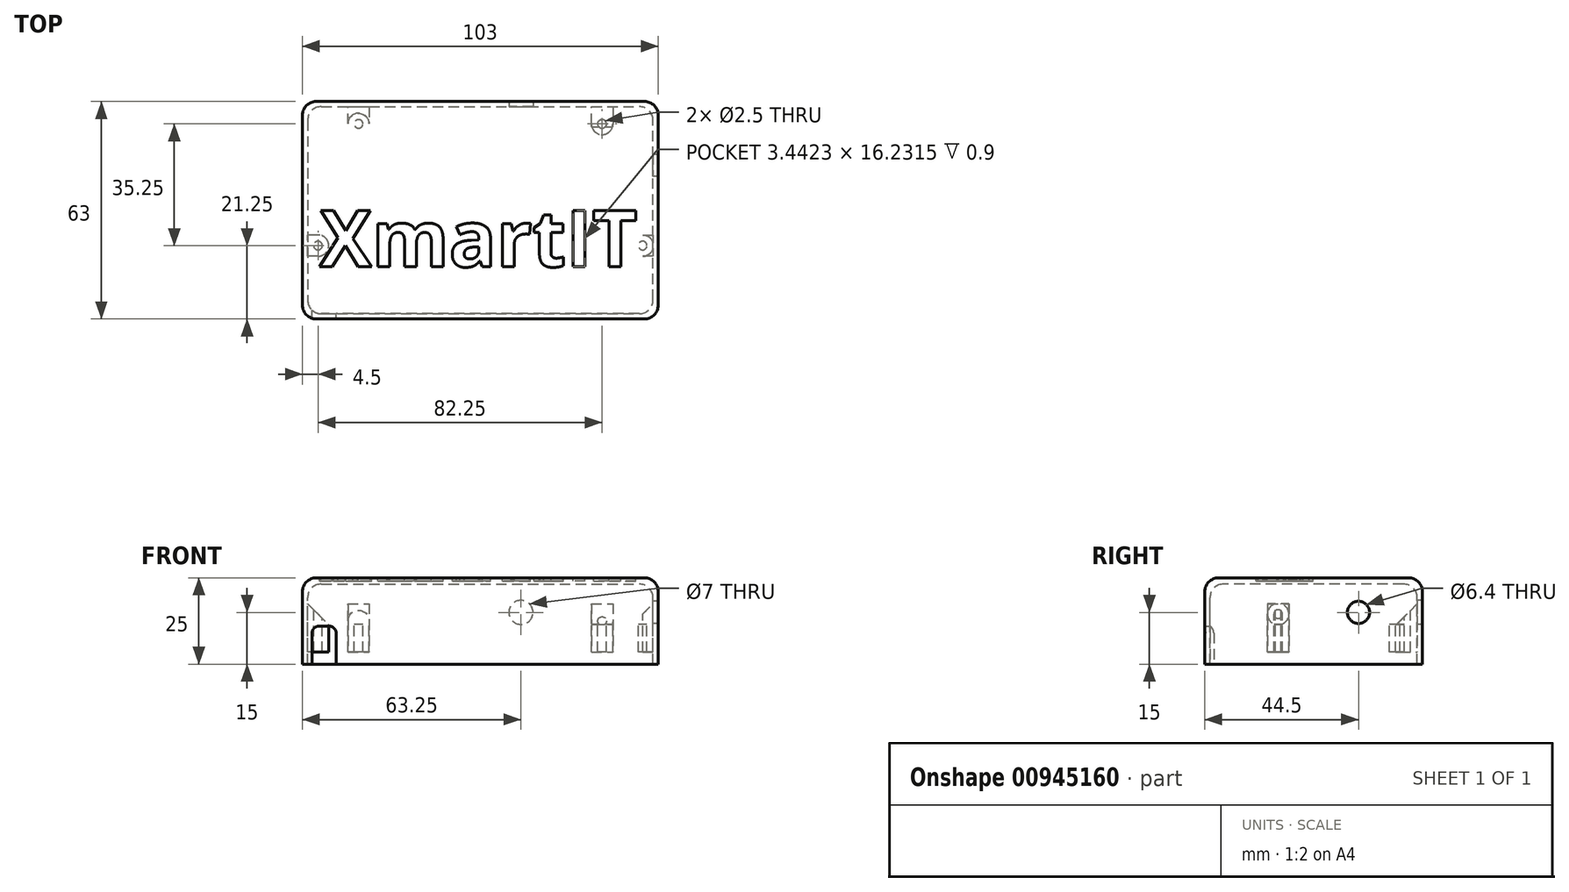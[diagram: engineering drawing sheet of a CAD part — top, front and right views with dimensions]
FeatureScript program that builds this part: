
annotation { "Feature Type Name" : "Feature", "Feature Type Description" : "" }
export const myFeature = defineFeature(function(context is Context, id is Id, definition is map)
    precondition{}
    {
        {
            assignVariable(context, id + "F0", {"name" : "Paredes", "anyValue" : 1.5});
        }
        {
            var Q0;
            Q0=qCreatedBy(makeId("Top.planeOp"),FACE);
            var sketch = newSketch(context, id + "F1", { "sketchPlane" : qUnion([Q0])});
            skLineSegment(sketch, "E0.bottom", {"start": v(50, -30) * mm, "end": v(-50, -30) * mm});
            skLineSegment(sketch, "E0.top", {"start": v(50, 30) * mm, "end": v(-50, 30) * mm});
            skLineSegment(sketch, "E0.left", {"start": v(50, -30) * mm, "end": v(50, 30) * mm});
            skLineSegment(sketch, "E0.right", {"start": v(-50, -30) * mm, "end": v(-50, 30) * mm});
            skPoint(sketch, "E0.middle", {"position": v(0, 0) * mm});
            skLineSegment(sketch, "E1.bottom", {"start": v(51.5, -31.5) * mm, "end": v(-51.5, -31.5) * mm});
            skLineSegment(sketch, "E1.top", {"start": v(51.5, 31.5) * mm, "end": v(-51.5, 31.5) * mm});
            skLineSegment(sketch, "E1.left", {"start": v(51.5, -31.5) * mm, "end": v(51.5, 31.5) * mm});
            skLineSegment(sketch, "E1.right", {"start": v(-51.5, -31.5) * mm, "end": v(-51.5, 31.5) * mm});
            skLineSegment(sketch, "E2.bottom", {"start": v(72.1, -40) * mm, "end": v(-72.1, -40) * mm});
            skLineSegment(sketch, "E2.top", {"start": v(72.1, 40) * mm, "end": v(-72.1, 40) * mm});
            skLineSegment(sketch, "E2.left", {"start": v(72.1, -40) * mm, "end": v(72.1, 40) * mm});
            skLineSegment(sketch, "E2.right", {"start": v(-72.1, -40) * mm, "end": v(-72.1, 40) * mm});
            skLineSegment(sketch, "E3", {"start": v(-51.5, 31.5) * mm, "end": v(-51.5, 40) * mm});
            skLineSegment(sketch, "E4", {"start": v(-51.5, -31.5) * mm, "end": v(-51.5, -40) * mm});
            skLineSegment(sketch, "E5", {"start": v(-41.73, -30) * mm, "end": v(-41.73, -4) * mm, "construction": true});
            skLineSegment(sketch, "E6.bottom", {"start": v(-50, -4) * mm, "end": v(50, -4) * mm});
            skLineSegment(sketch, "E6.top", {"start": v(-50, -2.2) * mm, "end": v(50, -2.2) * mm});
            skLineSegment(sketch, "E6.left", {"start": v(-50, -4) * mm, "end": v(-50, -2.2) * mm});
            skLineSegment(sketch, "E6.right", {"start": v(50, -4) * mm, "end": v(50, -2.2) * mm});
            skLineSegment(sketch, "E7.bottom", {"start": v(-55.7, -5) * mm, "end": v(-51.5, -5) * mm});
            skLineSegment(sketch, "E7.top", {"start": v(-55.7, 5) * mm, "end": v(-51.5, 5) * mm});
            skLineSegment(sketch, "E7.left", {"start": v(-55.7, -5) * mm, "end": v(-55.7, 5) * mm});
            skPoint(sketch, "E7.middle", {"position": v(-51.5, 0) * mm});
            skPoint(sketch, "E7.right.start.orphan", {"position": v(-47.3, -5) * mm});
            skPoint(sketch, "E8.trimOffspring.end.orphan", {"position": v(-47.3, 5) * mm});
            skLineSegment(sketch, "E9.bottom", {"start": v(72.1, -40) * mm, "end": v(84.1, -40) * mm});
            skLineSegment(sketch, "E9.top", {"start": v(72.1, -28) * mm, "end": v(84.1, -28) * mm});
            skLineSegment(sketch, "E9.left", {"start": v(72.1, -40) * mm, "end": v(72.1, -28) * mm});
            skLineSegment(sketch, "E9.right", {"start": v(87.1, -37) * mm, "end": v(87.1, -31) * mm});
            skCircle(sketch, "E10", {"center": v(79.6, -34) * mm, "radius": 1.5 * mm});
            skPoint(sketch, "E10.centerSnap0", {"position": v(87.1, -34) * mm});
            skPoint(sketch, "E10.centerSnap1", {"position": v(79.6, -28) * mm});
            skPoint(sketch, "E11.visualSharp", {"position": v(87.1, -28) * mm});
            skArc(sketch, "E11.filletArc", {"start": v(87.1, -31) * mm, "mid": v(86.22, -28.88) * mm, "end": v(84.1, -28) * mm});
            skPoint(sketch, "E12.visualSharp", {"position": v(87.1, -40) * mm});
            skArc(sketch, "E12.filletArc", {"start": v(84.1, -40) * mm, "mid": v(86.22, -39.12) * mm, "end": v(87.1, -37) * mm});
            skLineSegment(sketch, "E13", {"start": v(0, 0) * mm, "end": v(11.58, 0) * mm, "construction": true});
            skLineSegment(sketch, "E14.MirrorCS", {"start": v(87.1, 37) * mm, "end": v(87.1, 31) * mm});
            skPoint(sketch, "E15.MirrorP", {"position": v(79.6, 28) * mm});
            skCircle(sketch, "E16.MirrorC", {"center": v(79.6, 34) * mm, "radius": 1.5 * mm});
            skLineSegment(sketch, "E17.MirrorCS", {"start": v(72.1, 28) * mm, "end": v(84.1, 28) * mm});
            skPoint(sketch, "E18.MirrorP", {"position": v(87.1, 28) * mm});
            skArc(sketch, "E19.MirrorCS", {"start": v(87.1, 31) * mm, "mid": v(86.22, 28.88) * mm, "end": v(84.1, 28) * mm});
            skPoint(sketch, "E20.MirrorP", {"position": v(87.1, 40) * mm});
            skLineSegment(sketch, "E21.MirrorCS", {"start": v(72.1, 40) * mm, "end": v(84.1, 40) * mm});
            skPoint(sketch, "E22.MirrorP", {"position": v(87.1, 34) * mm});
            skArc(sketch, "E23.MirrorCS", {"start": v(84.1, 40) * mm, "mid": v(86.22, 39.12) * mm, "end": v(87.1, 37) * mm});
            skLineSegment(sketch, "E24", {"start": v(0, 31.5) * mm, "end": v(0, 40) * mm});
            skLineSegment(sketch, "E25", {"start": v(16, -31.5) * mm, "end": v(16, -38.7) * mm});
            skLineSegment(sketch, "E26", {"start": v(16, -38.7) * mm, "end": v(-51.5, -38.7) * mm});
            skLineSegment(sketch, "E27", {"start": v(16, -38.7) * mm, "end": v(16, -40) * mm});
            skSolve(sketch);
        }
        {
            var Q0;
            {var subQ10=sQuery(id+"F1.wireOp",EDGE,"E0.bottom");Q0=makeQuery(id+"F1.imprint","IMPRINT",FACE,{"disambiguationData":[TD([[makeQuery(id+"F1.imprint","IMPRINT",EDGE,{"derivedFrom":subQ10}),1.0]])]});}
            extrude(context, id + "F2", {"entities" : qUnion([Q0]), "oppositeDirection" : true, "depth" : 25 * mm, "offsetDistance" : 25 * mm});
        }
        {
            var Q0;
            {var subQ0=sQuery(id+"F1.wireOp",EDGE,"E0.bottom");Q0=makeQuery(id+"F1.imprint","IMPRINT",FACE,{"disambiguationData":[TD([[makeQuery(id+"F1.imprint","IMPRINT",EDGE,{"derivedFrom":subQ0}),-1.0]])]});}
            var Q1;
            {var subQ10=sQuery(id+"F1.wireOp",EDGE,"E0.bottom");Q1=makeQuery(id+"F1.imprint","IMPRINT",FACE,{"disambiguationData":[TD([[makeQuery(id+"F1.imprint","IMPRINT",EDGE,{"derivedFrom":subQ10}),1.0]])]});}
            var Q2;
            {var subQ0=sQuery(id+"F1.wireOp",EDGE,"E0.top");Q2=makeQuery(id+"F1.imprint","IMPRINT",FACE,{"disambiguationData":[TD([[makeQuery(id+"F1.imprint","IMPRINT",EDGE,{"derivedFrom":subQ0}),1.0]])]});}
            var Q3;
            {var subQ2=sQuery(id+"F1.wireOp",EDGE,"E6.bottom");Q3=makeQuery(id+"F1.imprint","IMPRINT",FACE,{"disambiguationData":[TD([[makeQuery(id+"F1.imprint","IMPRINT",EDGE,{"derivedFrom":subQ2}),1.0]])]});}
            extrude(context, id + "F3", {"entities" : qUnion([Q0, Q1, Q2, Q3]), "operationType" : NewBodyOperationType.ADD, "oppositeDirection" : true, "depth" : 1.8 * mm, "offsetDistance" : 25 * mm});
        }
        {
            var Q0;
            Q0=makeQuery(id+"F2.opExtrude","SWEPT_FACE",FACE,{"disambiguationData":[OSD([sQuery(id+"F1.wireOp",EDGE,"E1.left")])]});
            cPlane(context, id + "F4", {"entities" : qUnion([Q0]), "cplaneType" : CPlaneType.OFFSET, "offset" : (getVariable(context, 'Paredes')) * mm, "oppositeDirection" : true, "width" : 150 * mm, "height" : 150 * mm});
        }
        {
            var Q0;
            Q0=qCreatedBy(id+"F4.planeOp",FACE);
            var sketch = newSketch(context, id + "F5", { "sketchPlane" : qUnion([Q0])});
            skLineSegment(sketch, "E28", {"start": v(0, 0) * mm, "end": v(0, -10) * mm, "construction": true});
            skLineSegment(sketch, "E29", {"start": v(0, -10) * mm, "end": v(13, -10) * mm, "construction": true});
            skCircle(sketch, "E30", {"center": v(13, -10) * mm, "radius": 3.2 * mm});
            skCircle(sketch, "E31", {"center": v(13, -10) * mm, "radius": 4.75 * mm});
            skSolve(sketch);
        }
        {
            var Q0;
            Q0=makeQuery(id+"F5.imprint","IMPRINT",FACE,{"disambiguationData":[TD([[makeQuery(id+"F5.imprint","IMPRINT",EDGE,{"derivedFrom":sQuery(id+"F5.wireOp",EDGE,"E30")}),1.0]])]});
            var Q1;
            Q1=makeQuery(id+"F2.opExtrude","SWEPT_FACE",FACE,{"disambiguationData":[OSD([sQuery(id+"F1.wireOp",EDGE,"E1.left")])]});
            extrude(context, id + "F6", {"entities" : qUnion([Q0]), "operationType" : NewBodyOperationType.REMOVE, "endBound" : BoundingType.UP_TO_NEXT, "depth" : 35 * mm, "endBoundEntityFace" : qUnion([Q1]), "offsetDistance" : 10 * mm, "offsetOppositeDirection" : true});
        }
        {
            var Q0;
            Q0=makeQuery(id+"F5.imprint","IMPRINT",FACE,{"disambiguationData":[TD([[makeQuery(id+"F5.imprint","IMPRINT",EDGE,{"derivedFrom":sQuery(id+"F5.wireOp",EDGE,"E30")}),-1.0]])]});
            var Q1;
            Q1=makeQuery(id+"F5.imprint","IMPRINT",FACE,{"disambiguationData":[TD([[makeQuery(id+"F5.imprint","IMPRINT",EDGE,{"derivedFrom":sQuery(id+"F5.wireOp",EDGE,"E30")}),1.0]])]});
            extrude(context, id + "F7", {"entities" : qUnion([Q0, Q1]), "operationType" : NewBodyOperationType.REMOVE, "oppositeDirection" : true, "depth" : 35 * mm, "offsetDistance" : 25 * mm});
        }
        {
            var Q0;
            Q0=qCreatedBy(makeId("Front.planeOp"),FACE);
            var sketch = newSketch(context, id + "F8", { "sketchPlane" : qUnion([Q0])});
            skLineSegment(sketch, "E32", {"start": v(0, 0) * mm, "end": v(0, -10) * mm, "construction": true});
            skLineSegment(sketch, "E33", {"start": v(0, -10) * mm, "end": v(11.75, -10) * mm, "construction": true});
            skCircle(sketch, "E34", {"center": v(11.75, -10) * mm, "radius": 3.5 * mm});
            skCircle(sketch, "E35.MirrorC", {"center": v(-11.75, -10) * mm, "radius": 3.5 * mm});
            skLineSegment(sketch, "E36", {"start": v(-11.75, -10) * mm, "end": v(-35.25, -10) * mm, "construction": true});
            skCircle(sketch, "E37", {"center": v(-35.25, -10) * mm, "radius": 3.5 * mm});
            skLineSegment(sketch, "E38", {"start": v(-35.25, -10) * mm, "end": v(-38.75, -10) * mm, "construction": true});
            skLineSegment(sketch, "E39", {"start": v(-38.75, -10) * mm, "end": v(-41.75, -10) * mm, "construction": true});
            skLineSegment(sketch, "E40", {"start": v(-41.75, -10) * mm, "end": v(-41.75, -14) * mm, "construction": true});
            skLineSegment(sketch, "E41.bottom", {"start": v(-41.75, -14) * mm, "end": v(-48.75, -14) * mm});
            skLineSegment(sketch, "E41.top", {"start": v(-41.75, -25) * mm, "end": v(-48.75, -25) * mm});
            skLineSegment(sketch, "E41.left", {"start": v(-41.75, -14) * mm, "end": v(-41.75, -25) * mm});
            skLineSegment(sketch, "E41.right", {"start": v(-48.75, -14) * mm, "end": v(-48.75, -25) * mm});
            skCircle(sketch, "E42.MirrorC", {"center": v(35.25, -10) * mm, "radius": 3.5 * mm});
            skSolve(sketch);
        }
        {
            var Q0;
            Q0=makeQuery(id+"F8.imprint","IMPRINT",FACE,{"disambiguationData":[TD([[makeQuery(id+"F8.imprint","IMPRINT",EDGE,{"derivedFrom":sQuery(id+"F8.wireOp",EDGE,"E34")}),1.0]])]});
            var Q1;
            Q1=makeQuery(id+"F8.imprint","IMPRINT",FACE,{"disambiguationData":[TD([[makeQuery(id+"F8.imprint","IMPRINT",EDGE,{"derivedFrom":sQuery(id+"F8.wireOp",EDGE,"E35.MirrorC")}),-1.0]])]});
            extrude(context, id + "F9", {"entities" : qUnion([Q0, Q1]), "operationType" : NewBodyOperationType.REMOVE, "endBound" : BoundingType.THROUGH_ALL, "oppositeDirection" : true, "depth" : 25 * mm, "offsetDistance" : 25 * mm});
        }
        {
            var Q0;
            Q0=makeQuery(id+"F8.imprint","IMPRINT",FACE,{"disambiguationData":[TD([[makeQuery(id+"F8.imprint","IMPRINT",EDGE,{"derivedFrom":sQuery(id+"F8.wireOp",EDGE,"E41.bottom")}),1.0]])]});
            extrude(context, id + "F10", {"entities" : qUnion([Q0]), "operationType" : NewBodyOperationType.REMOVE, "endBound" : BoundingType.THROUGH_ALL, "depth" : 25 * mm, "offsetDistance" : 25 * mm});
        }
        {
            var Q0;
            Q0=makeQuery(id+"F10.boolean.opBoolean","COPY",EDGE,{"derivedFrom":makeQuery(id+"F10.opExtrude","SWEPT_EDGE",EDGE,{"disambiguationData":[OSD([sQuery(id+"F8.wireOp",EDGE,"E41.bottom"),sQuery(id+"F8.wireOp",EDGE,"E41.right")])]})});
            var Q1;
            Q1=makeQuery(id+"F10.boolean.opBoolean","COPY",EDGE,{"derivedFrom":makeQuery(id+"F10.opExtrude","SWEPT_EDGE",EDGE,{"disambiguationData":[OSD([sQuery(id+"F8.wireOp",EDGE,"E41.bottom"),sQuery(id+"F8.wireOp",EDGE,"E41.left")])]})});
            fillet(context, id + "F11", {"entities" : qUnion([Q0, Q1]), "radius" : 2 * mm, "tangentPropagation" : true, "allowEdgeOverflow" : false});
        }
        {
            var Q0;
            {var subQ0=sQuery(id+"F1.wireOp",EDGE,"E1.right");var subQ1=sQuery(id+"F1.wireOp",EDGE,"E1.left");var subQ2=sQuery(id+"F1.wireOp",EDGE,"E1.top");var subQ3=sQuery(id+"F1.wireOp",EDGE,"E1.bottom");Q0=makeQuery(id+"F3.boolean.opBoolean","MERGE",FACE,{"derivedFrom":[makeQuery(id+"F2.opExtrude","CAP_FACE",FACE,{"disambiguationData":[OSD([sQuery(id+"F1.wireOp",EDGE,"E0.bottom"),sQuery(id+"F1.wireOp",EDGE,"E0.top"),sQuery(id+"F1.wireOp",EDGE,"E0.left"),sQuery(id+"F1.wireOp",EDGE,"E0.right"),subQ3,subQ2,subQ1,subQ0])],"isStart":true}),makeQuery(id+"F3.opExtrude","CAP_FACE",FACE,{"disambiguationData":[OSD([subQ3,subQ2,subQ1,subQ0])],"isStart":true})]});}
            cPlane(context, id + "F12", {"entities" : qUnion([Q0]), "cplaneType" : CPlaneType.OFFSET, "offset" : 13.5 * mm, "oppositeDirection" : true, "width" : 150 * mm, "height" : 150 * mm});
        }
        {
            var Q0;
            Q0=qCreatedBy(id+"F12.planeOp",FACE);
            var sketch = newSketch(context, id + "F13", { "sketchPlane" : qUnion([Q0])});
            skLineSegment(sketch, "E43", {"start": v(0, 0) * mm, "end": v(0, 0) * mm});
            skLineSegment(sketch, "E44", {"start": v(0, 0) * mm, "end": v(0, 1.5) * mm, "construction": true});
            skCircle(sketch, "E45", {"center": v(0, 1.5) * mm, "radius": 1.25 * mm});
            skCircle(sketch, "E46", {"center": v(0, 1.5) * mm, "radius": 3.1 * mm});
            skCircle(sketch, "E47.0.1.0", {"center": v(0, 13.25) * mm, "radius": 3.1 * mm});
            skCircle(sketch, "E47.0.1.1", {"center": v(0, 13.25) * mm, "radius": 1.25 * mm});
            skCircle(sketch, "E47.0.2.0", {"center": v(0, 25) * mm, "radius": 3.1 * mm});
            skCircle(sketch, "E47.0.2.1", {"center": v(0, 25) * mm, "radius": 1.25 * mm});
            skCircle(sketch, "E47.1.0.0", {"center": v(11.75, 1.5) * mm, "radius": 3.1 * mm});
            skCircle(sketch, "E47.1.0.1", {"center": v(11.75, 1.5) * mm, "radius": 1.25 * mm});
            skCircle(sketch, "E47.1.1.0", {"center": v(11.75, 13.25) * mm, "radius": 3.1 * mm});
            skCircle(sketch, "E47.1.1.1", {"center": v(11.75, 13.25) * mm, "radius": 1.25 * mm});
            skCircle(sketch, "E47.1.2.0", {"center": v(11.75, 25) * mm, "radius": 3.1 * mm});
            skCircle(sketch, "E47.1.2.1", {"center": v(11.75, 25) * mm, "radius": 1.25 * mm});
            skCircle(sketch, "E47.2.0.0", {"center": v(23.5, 1.5) * mm, "radius": 3.1 * mm});
            skCircle(sketch, "E47.2.0.1", {"center": v(23.5, 1.5) * mm, "radius": 1.25 * mm});
            skCircle(sketch, "E47.2.1.0", {"center": v(23.5, 13.25) * mm, "radius": 3.1 * mm});
            skCircle(sketch, "E47.2.1.1", {"center": v(23.5, 13.25) * mm, "radius": 1.25 * mm});
            skCircle(sketch, "E47.2.2.0", {"center": v(23.5, 25) * mm, "radius": 3.1 * mm});
            skCircle(sketch, "E47.2.2.1", {"center": v(23.5, 25) * mm, "radius": 1.25 * mm});
            skCircle(sketch, "E47.3.0.0", {"center": v(35.25, 1.5) * mm, "radius": 3.1 * mm});
            skCircle(sketch, "E47.3.0.1", {"center": v(35.25, 1.5) * mm, "radius": 1.25 * mm});
            skCircle(sketch, "E47.3.1.0", {"center": v(35.25, 13.25) * mm, "radius": 3.1 * mm});
            skCircle(sketch, "E47.3.1.1", {"center": v(35.25, 13.25) * mm, "radius": 1.25 * mm});
            skCircle(sketch, "E47.3.2.0", {"center": v(35.25, 25) * mm, "radius": 3.1 * mm});
            skCircle(sketch, "E47.3.2.1", {"center": v(35.25, 25) * mm, "radius": 1.25 * mm});
            skCircle(sketch, "E47.4.0.0", {"center": v(47, 1.5) * mm, "radius": 3.1 * mm});
            skCircle(sketch, "E47.4.0.1", {"center": v(47, 1.5) * mm, "radius": 1.25 * mm});
            skCircle(sketch, "E47.4.1.0", {"center": v(47, 13.25) * mm, "radius": 3.1 * mm});
            skCircle(sketch, "E47.4.1.1", {"center": v(47, 13.25) * mm, "radius": 1.25 * mm});
            skCircle(sketch, "E47.4.2.0", {"center": v(47, 25) * mm, "radius": 3.1 * mm});
            skCircle(sketch, "E47.4.2.1", {"center": v(47, 25) * mm, "radius": 1.25 * mm});
            skLineSegment(sketch, "E47.direction1", {"start": v(0, 1.5) * mm, "end": v(11.75, 1.5) * mm, "construction": true});
            skLineSegment(sketch, "E47.direction2", {"start": v(0, 1.5) * mm, "end": v(0, 13.25) * mm, "construction": true});
            skCircle(sketch, "E48.MirrorC", {"center": v(-11.75, 1.5) * mm, "radius": 1.25 * mm});
            skCircle(sketch, "E49.MirrorC", {"center": v(-35.25, 25) * mm, "radius": 1.25 * mm});
            skCircle(sketch, "E50.MirrorC", {"center": v(-47, 25) * mm, "radius": 1.25 * mm});
            skCircle(sketch, "E51.MirrorC", {"center": v(-11.75, 25) * mm, "radius": 1.25 * mm});
            skCircle(sketch, "E52.MirrorC", {"center": v(-47, 1.5) * mm, "radius": 1.25 * mm});
            skCircle(sketch, "E53.MirrorC", {"center": v(-47, 13.25) * mm, "radius": 1.25 * mm});
            skCircle(sketch, "E54.MirrorC", {"center": v(-11.75, 13.25) * mm, "radius": 1.25 * mm});
            skCircle(sketch, "E55.MirrorC", {"center": v(-23.5, 25) * mm, "radius": 1.25 * mm});
            skCircle(sketch, "E56.MirrorC", {"center": v(-23.5, 1.5) * mm, "radius": 1.25 * mm});
            skCircle(sketch, "E57.MirrorC", {"center": v(-35.25, 1.5) * mm, "radius": 1.25 * mm});
            skCircle(sketch, "E58.MirrorC", {"center": v(-35.25, 13.25) * mm, "radius": 1.25 * mm});
            skCircle(sketch, "E59.MirrorC", {"center": v(-23.5, 13.25) * mm, "radius": 1.25 * mm});
            skCircle(sketch, "E60.MirrorC", {"center": v(-11.75, 13.25) * mm, "radius": 3.1 * mm});
            skCircle(sketch, "E61.MirrorC", {"center": v(-35.25, 25) * mm, "radius": 3.1 * mm});
            skCircle(sketch, "E62.MirrorC", {"center": v(-47, 25) * mm, "radius": 3.1 * mm});
            skCircle(sketch, "E63.MirrorC", {"center": v(-35.25, 1.5) * mm, "radius": 3.1 * mm});
            skCircle(sketch, "E64.MirrorC", {"center": v(-47, 13.25) * mm, "radius": 3.1 * mm});
            skCircle(sketch, "E65.MirrorC", {"center": v(-23.5, 25) * mm, "radius": 3.1 * mm});
            skCircle(sketch, "E66.MirrorC", {"center": v(-11.75, 1.5) * mm, "radius": 3.1 * mm});
            skCircle(sketch, "E67.MirrorC", {"center": v(-35.25, 13.25) * mm, "radius": 3.1 * mm});
            skCircle(sketch, "E68.MirrorC", {"center": v(-47, 1.5) * mm, "radius": 3.1 * mm});
            skCircle(sketch, "E69.MirrorC", {"center": v(-11.75, 25) * mm, "radius": 3.1 * mm});
            skCircle(sketch, "E70.MirrorC", {"center": v(-23.5, 1.5) * mm, "radius": 3.1 * mm});
            skCircle(sketch, "E71.MirrorC", {"center": v(-23.5, 13.25) * mm, "radius": 3.1 * mm});
            skCircle(sketch, "E72.MirrorC", {"center": v(-47, -10.25) * mm, "radius": 3.1 * mm});
            skCircle(sketch, "E73.MirrorC", {"center": v(-47, -10.25) * mm, "radius": 1.25 * mm});
            skLineSegment(sketch, "E74", {"start": v(-47, -10.25) * mm, "end": v(-47, -7.15) * mm, "construction": true});
            skLineSegment(sketch, "E75", {"start": v(-47, -7.15) * mm, "end": v(-50.1, -7.15) * mm});
            skLineSegment(sketch, "E76", {"start": v(-47, -10.25) * mm, "end": v(-50.1, -10.25) * mm, "construction": true});
            skLineSegment(sketch, "E77", {"start": v(-50.1, -10.25) * mm, "end": v(-50.1, -7.15) * mm});
            skLineSegment(sketch, "E78.MirrorCS", {"start": v(-47, -13.35) * mm, "end": v(-50.1, -13.35) * mm});
            skLineSegment(sketch, "E79.MirrorCS", {"start": v(-50.1, -10.25) * mm, "end": v(-50.1, -13.35) * mm});
            skLineSegment(sketch, "E80", {"start": v(35.25, 25) * mm, "end": v(32.15, 25) * mm, "construction": true});
            skLineSegment(sketch, "E81", {"start": v(32.15, 25) * mm, "end": v(32.15, 30.06) * mm});
            skLineSegment(sketch, "E82", {"start": v(32.15, 30.06) * mm, "end": v(38.35, 30.06) * mm});
            skLineSegment(sketch, "E83", {"start": v(35.25, 25) * mm, "end": v(38.35, 25) * mm, "construction": true});
            skLineSegment(sketch, "E84", {"start": v(38.35, 25) * mm, "end": v(38.35, 30.06) * mm});
            skLineSegment(sketch, "E85", {"start": v(-47, -10.25) * mm, "end": v(-43.9, -10.25) * mm, "construction": true});
            skLineSegment(sketch, "E86", {"start": v(-43.9, -10.25) * mm, "end": v(-39.9, -10.25) * mm, "construction": true});
            skLineSegment(sketch, "E87", {"start": v(-39.9, -10.25) * mm, "end": v(-39.9, -30.05) * mm});
            skLineSegment(sketch, "E88", {"start": v(-39.9, -30.05) * mm, "end": v(-38.1, -30.05) * mm});
            skLineSegment(sketch, "E89", {"start": v(-38.1, -30.05) * mm, "end": v(-38.1, -10.25) * mm});
            skLineSegment(sketch, "E90", {"start": v(-38.1, -10.25) * mm, "end": v(-39.9, -10.25) * mm});
            skLineSegment(sketch, "E91.MirrorCS", {"start": v(-32.15, 25) * mm, "end": v(-32.15, 30.06) * mm});
            skLineSegment(sketch, "E92.MirrorCS", {"start": v(-38.35, 25) * mm, "end": v(-38.35, 30.06) * mm});
            skCircle(sketch, "E93.MirrorC", {"center": v(47, -10.25) * mm, "radius": 3.1 * mm});
            skLineSegment(sketch, "E94.MirrorCS", {"start": v(47, -13.35) * mm, "end": v(50.1, -13.35) * mm});
            skLineSegment(sketch, "E95.MirrorCS", {"start": v(47, -7.15) * mm, "end": v(50.1, -7.15) * mm});
            skCircle(sketch, "E96.MirrorC", {"center": v(47, -10.25) * mm, "radius": 1.25 * mm});
            skLineSegment(sketch, "E97.MirrorCS", {"start": v(-32.15, 30.06) * mm, "end": v(-38.35, 30.06) * mm});
            skLineSegment(sketch, "E98.MirrorCS", {"start": v(50.1, -10.25) * mm, "end": v(50.1, -13.35) * mm});
            skLineSegment(sketch, "E99.MirrorCS", {"start": v(50.1, -10.25) * mm, "end": v(50.1, -7.15) * mm});
            skSolve(sketch);
        }
        {
            var Q0;
            Q0=makeQuery(id+"F13.imprint","IMPRINT",FACE,{"disambiguationData":[TD([[makeQuery(id+"F13.imprint","IMPRINT",EDGE,{"derivedFrom":sQuery(id+"F13.wireOp",EDGE,"E47.3.2.0")}),1.0]])]});
            var Q1;
            {var subQ0=sQuery(id+"F13.wireOp",EDGE,"E81");Q1=makeQuery(id+"F13.imprint","IMPRINT",FACE,{"disambiguationData":[TD([[makeQuery(id+"F13.imprint","IMPRINT",EDGE,{"derivedFrom":subQ0}),-1.0]])]});}
            var Q2;
            {var subQ0=sQuery(id+"F13.wireOp",EDGE,"E91.MirrorCS");Q2=makeQuery(id+"F13.imprint","IMPRINT",FACE,{"disambiguationData":[TD([[makeQuery(id+"F13.imprint","IMPRINT",EDGE,{"derivedFrom":subQ0}),1.0]])]});}
            var Q3;
            Q3=makeQuery(id+"F13.imprint","IMPRINT",FACE,{"disambiguationData":[TD([[makeQuery(id+"F13.imprint","IMPRINT",EDGE,{"derivedFrom":sQuery(id+"F13.wireOp",EDGE,"E49.MirrorC")}),1.0]])]});
            var Q4;
            {var subQ2=sQuery(id+"F13.wireOp",EDGE,"E78.MirrorCS");Q4=makeQuery(id+"F13.imprint","IMPRINT",FACE,{"disambiguationData":[TD([[makeQuery(id+"F13.imprint","IMPRINT",EDGE,{"derivedFrom":subQ2}),-1.0]])]});}
            var Q5;
            Q5=makeQuery(id+"F13.imprint","IMPRINT",FACE,{"disambiguationData":[TD([[makeQuery(id+"F13.imprint","IMPRINT",EDGE,{"derivedFrom":sQuery(id+"F13.wireOp",EDGE,"E73.MirrorC")}),-1.0]])]});
            var Q6;
            {var subQ0=sQuery(id+"F13.wireOp",EDGE,"E75");Q6=makeQuery(id+"F13.imprint","IMPRINT",FACE,{"disambiguationData":[TD([[makeQuery(id+"F13.imprint","IMPRINT",EDGE,{"derivedFrom":subQ0}),1.0]])]});}
            var Q7;
            {var subQ0=sQuery(id+"F13.wireOp",EDGE,"E95.MirrorCS");Q7=makeQuery(id+"F13.imprint","IMPRINT",FACE,{"disambiguationData":[TD([[makeQuery(id+"F13.imprint","IMPRINT",EDGE,{"derivedFrom":subQ0}),-1.0]])]});}
            var Q8;
            Q8=makeQuery(id+"F13.imprint","IMPRINT",FACE,{"disambiguationData":[TD([[makeQuery(id+"F13.imprint","IMPRINT",EDGE,{"derivedFrom":sQuery(id+"F13.wireOp",EDGE,"E96.MirrorC")}),1.0]])]});
            var Q9;
            {var subQ0=sQuery(id+"F13.wireOp",EDGE,"E94.MirrorCS");Q9=makeQuery(id+"F13.imprint","IMPRINT",FACE,{"disambiguationData":[TD([[makeQuery(id+"F13.imprint","IMPRINT",EDGE,{"derivedFrom":subQ0}),1.0]])]});}
            extrude(context, id + "F14", {"entities" : qUnion([Q0, Q1, Q2, Q3, Q4, Q5, Q6, Q7, Q8, Q9]), "operationType" : NewBodyOperationType.ADD, "oppositeDirection" : true, "depth" : 8 * mm, "offsetDistance" : 25 * mm});
        }
        {
            var Q0;
            Q0=makeQuery(id+"F3.opExtrude","CAP_FACE",FACE,{"disambiguationData":[OSD([sQuery(id+"F1.wireOp",EDGE,"E1.bottom"),sQuery(id+"F1.wireOp",EDGE,"E1.top"),sQuery(id+"F1.wireOp",EDGE,"E1.left"),sQuery(id+"F1.wireOp",EDGE,"E1.right")])],"isStart":false});
            var Q1;
            {var subQ0=sQuery(id+"F1.wireOp",EDGE,"E1.right");var subQ1=sQuery(id+"F1.wireOp",EDGE,"E1.left");var subQ2=sQuery(id+"F1.wireOp",EDGE,"E1.top");var subQ3=sQuery(id+"F1.wireOp",EDGE,"E1.bottom");Q1=makeQuery(id+"F3.boolean.opBoolean","MERGE",FACE,{"derivedFrom":[makeQuery(id+"F2.opExtrude","CAP_FACE",FACE,{"disambiguationData":[OSD([sQuery(id+"F1.wireOp",EDGE,"E0.bottom"),sQuery(id+"F1.wireOp",EDGE,"E0.top"),sQuery(id+"F1.wireOp",EDGE,"E0.left"),sQuery(id+"F1.wireOp",EDGE,"E0.right"),subQ3,subQ2,subQ1,subQ0])],"isStart":true}),makeQuery(id+"F3.opExtrude","CAP_FACE",FACE,{"disambiguationData":[OSD([subQ3,subQ2,subQ1,subQ0])],"isStart":true})]});}
            var Q2;
            Q2=makeQuery(id+"F2.opExtrude","SWEPT_EDGE",EDGE,{"disambiguationData":[OSD([sQuery(id+"F1.wireOp",EDGE,"E1.bottom"),sQuery(id+"F1.wireOp",EDGE,"E1.left")])]});
            var Q3;
            Q3=makeQuery(id+"F2.opExtrude","SWEPT_EDGE",EDGE,{"disambiguationData":[OSD([sQuery(id+"F1.wireOp",EDGE,"E1.top"),sQuery(id+"F1.wireOp",EDGE,"E1.left")])]});
            var Q4;
            Q4=makeQuery(id+"F2.opExtrude","SWEPT_EDGE",EDGE,{"disambiguationData":[OSD([sQuery(id+"F1.wireOp",EDGE,"E1.bottom"),sQuery(id+"F1.wireOp",EDGE,"E1.right"),sQuery(id+"F1.wireOp",EDGE,"E4")])]});
            var Q5;
            Q5=makeQuery(id+"F2.opExtrude","SWEPT_EDGE",EDGE,{"disambiguationData":[OSD([sQuery(id+"F1.wireOp",EDGE,"E1.top"),sQuery(id+"F1.wireOp",EDGE,"E1.right"),sQuery(id+"F1.wireOp",EDGE,"E3")])]});
            var Q6;
            Q6=makeQuery(id+"F2.opExtrude","SWEPT_EDGE",EDGE,{"disambiguationData":[OSD([sQuery(id+"F1.wireOp",EDGE,"E0.top"),sQuery(id+"F1.wireOp",EDGE,"E0.left")])]});
            var Q7;
            Q7=makeQuery(id+"F2.opExtrude","SWEPT_EDGE",EDGE,{"disambiguationData":[OSD([sQuery(id+"F1.wireOp",EDGE,"E0.top"),sQuery(id+"F1.wireOp",EDGE,"E0.right")])]});
            var Q8;
            Q8=makeQuery(id+"F2.opExtrude","SWEPT_EDGE",EDGE,{"disambiguationData":[OSD([sQuery(id+"F1.wireOp",EDGE,"E0.bottom"),sQuery(id+"F1.wireOp",EDGE,"E0.right")])]});
            var Q9;
            Q9=makeQuery(id+"F2.opExtrude","SWEPT_EDGE",EDGE,{"disambiguationData":[OSD([sQuery(id+"F1.wireOp",EDGE,"E0.bottom"),sQuery(id+"F1.wireOp",EDGE,"E0.left")])]});
            fillet(context, id + "F15", {"entities" : qUnion([Q0, Q1, Q2, Q3, Q4, Q5, Q6, Q7, Q8, Q9]), "radius" : 4 * mm, "tangentPropagation" : true, "allowEdgeOverflow" : false});
        }
        {
            var Q0;
            Q0=qCreatedBy(makeId("Top.planeOp"),FACE);
            var sketch = newSketch(context, id + "F16", { "sketchPlane" : qUnion([Q0])});
            skText(sketch, "E100", { "text": "XmartIT", "fontName": "OpenSans-Bold.ttf"});
            const initialGuessF16  = {"E100": [-0.04658, -0.01637, 1, 0, 0.01637]};
            skSetInitialGuess(sketch, initialGuessF16);
            skSolve(sketch);
        }
        {
            var Q0;
            Q0=qSketchRegion(id+"F16",true);
            extrude(context, id + "F17", {"entities" : qUnion([Q0]), "operationType" : NewBodyOperationType.REMOVE, "oppositeDirection" : true, "depth" : 0.9 * mm, "offsetDistance" : 25 * mm});
        }
        {
            var Q0;
            Q0=makeQuery(id+"F14.boolean.opBoolean","INTERSECT",EDGE,{"derivedFrom":[makeQuery(id+"F2.opExtrude","SWEPT_FACE",FACE,{"disambiguationData":[OSD([sQuery(id+"F1.wireOp",EDGE,"E0.left")])]}),makeQuery(id+"F14.opExtrude","CAP_FACE",FACE,{"disambiguationData":[OSD([sQuery(id+"F13.wireOp",EDGE,"E93.MirrorC"),sQuery(id+"F13.wireOp",EDGE,"E94.MirrorCS"),sQuery(id+"F13.wireOp",EDGE,"E95.MirrorCS"),sQuery(id+"F13.wireOp",EDGE,"E96.MirrorC"),sQuery(id+"F13.wireOp",EDGE,"E98.MirrorCS"),sQuery(id+"F13.wireOp",EDGE,"E99.MirrorCS")])],"isStart":true})]});
            var Q1;
            Q1=makeQuery(id+"F14.boolean.opBoolean","INTERSECT",EDGE,{"derivedFrom":[makeQuery(id+"F2.opExtrude","SWEPT_FACE",FACE,{"disambiguationData":[OSD([sQuery(id+"F1.wireOp",EDGE,"E0.right")])]}),makeQuery(id+"F14.opExtrude","CAP_FACE",FACE,{"disambiguationData":[OSD([sQuery(id+"F13.wireOp",EDGE,"E72.MirrorC"),sQuery(id+"F13.wireOp",EDGE,"E73.MirrorC"),sQuery(id+"F13.wireOp",EDGE,"E75"),sQuery(id+"F13.wireOp",EDGE,"E77"),sQuery(id+"F13.wireOp",EDGE,"E78.MirrorCS"),sQuery(id+"F13.wireOp",EDGE,"E79.MirrorCS")])],"isStart":true})]});
            var Q2;
            Q2=makeQuery(id+"F14.boolean.opBoolean","INTERSECT",EDGE,{"derivedFrom":[makeQuery(id+"F2.opExtrude","SWEPT_FACE",FACE,{"disambiguationData":[OSD([sQuery(id+"F1.wireOp",EDGE,"E0.top")])]}),makeQuery(id+"F14.opExtrude","CAP_FACE",FACE,{"disambiguationData":[OSD([sQuery(id+"F13.wireOp",EDGE,"E49.MirrorC"),sQuery(id+"F13.wireOp",EDGE,"E61.MirrorC"),sQuery(id+"F13.wireOp",EDGE,"E91.MirrorCS"),sQuery(id+"F13.wireOp",EDGE,"E92.MirrorCS"),sQuery(id+"F13.wireOp",EDGE,"E97.MirrorCS")])],"isStart":true})]});
            var Q3;
            Q3=makeQuery(id+"F14.boolean.opBoolean","INTERSECT",EDGE,{"derivedFrom":[makeQuery(id+"F2.opExtrude","SWEPT_FACE",FACE,{"disambiguationData":[OSD([sQuery(id+"F1.wireOp",EDGE,"E0.top")])]}),makeQuery(id+"F14.opExtrude","CAP_FACE",FACE,{"disambiguationData":[OSD([sQuery(id+"F13.wireOp",EDGE,"E47.3.2.0"),sQuery(id+"F13.wireOp",EDGE,"E47.3.2.1"),sQuery(id+"F13.wireOp",EDGE,"E81"),sQuery(id+"F13.wireOp",EDGE,"E82"),sQuery(id+"F13.wireOp",EDGE,"E84")])],"isStart":true})]});
            chamfer(context, id + "F18", {"entities" : qUnion([Q0, Q1, Q2, Q3]), "width" : 6 * mm, "tangentPropagation" : true});
        }
    });
